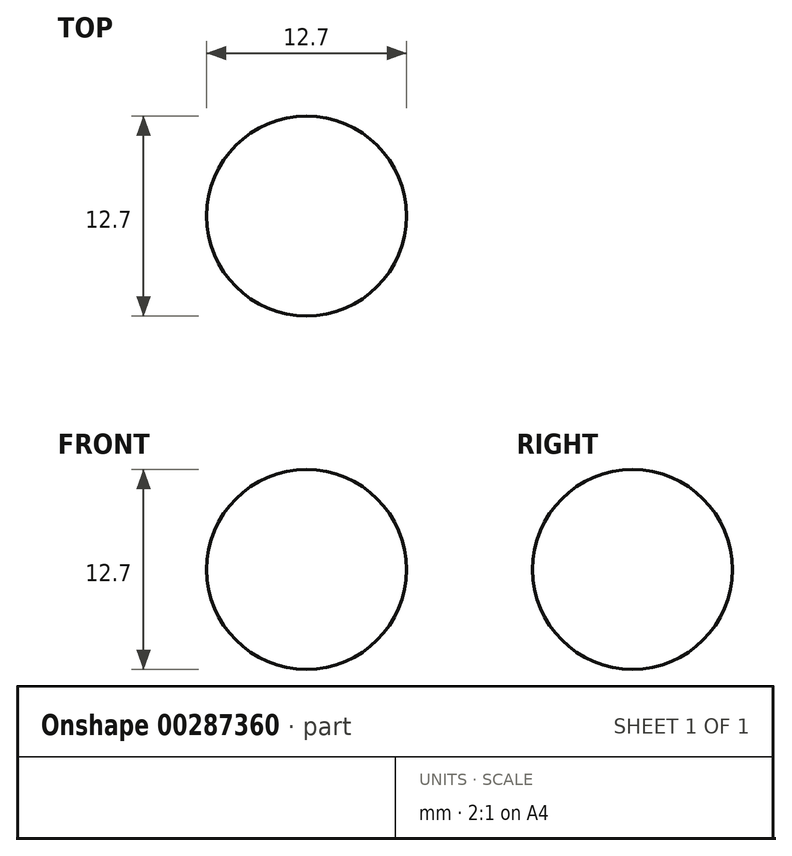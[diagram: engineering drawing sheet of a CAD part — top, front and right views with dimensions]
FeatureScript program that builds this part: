
annotation { "Feature Type Name" : "Feature", "Feature Type Description" : "" }
export const myFeature = defineFeature(function(context is Context, id is Id, definition is map)
    precondition{}
    {
        {
            var Q0;
            Q0=qCreatedBy(makeId("Top.planeOp"),FACE);
            var sketch = newSketch(context, id + "F0", { "sketchPlane" : qUnion([Q0])});
            skArc(sketch, "E0", {"start": v(0, -1.7) * mm, "mid": v(6.35, 4.64) * mm, "end": v(0, 11) * mm});
            skLineSegment(sketch, "E1", {"start": v(0, 11) * mm, "end": v(0, -1.7) * mm});
            skLineSegment(sketch, "E2", {"start": v(0, 16.42) * mm, "end": v(0, -3.46) * mm, "construction": true});
            skSolve(sketch);
        }
        {
            var Q0;
            Q0 = qSketchRegion(id + "F0", true);
            var Q1;
            Q1=sQuery(id+"F0.wireOp",EDGE,"E2");
            revolve(context, id + "F1", {"entities" : qUnion([Q0]), "axis" : qUnion([Q1]), "revolveType" : RevolveType.FULL});
        }
    });
